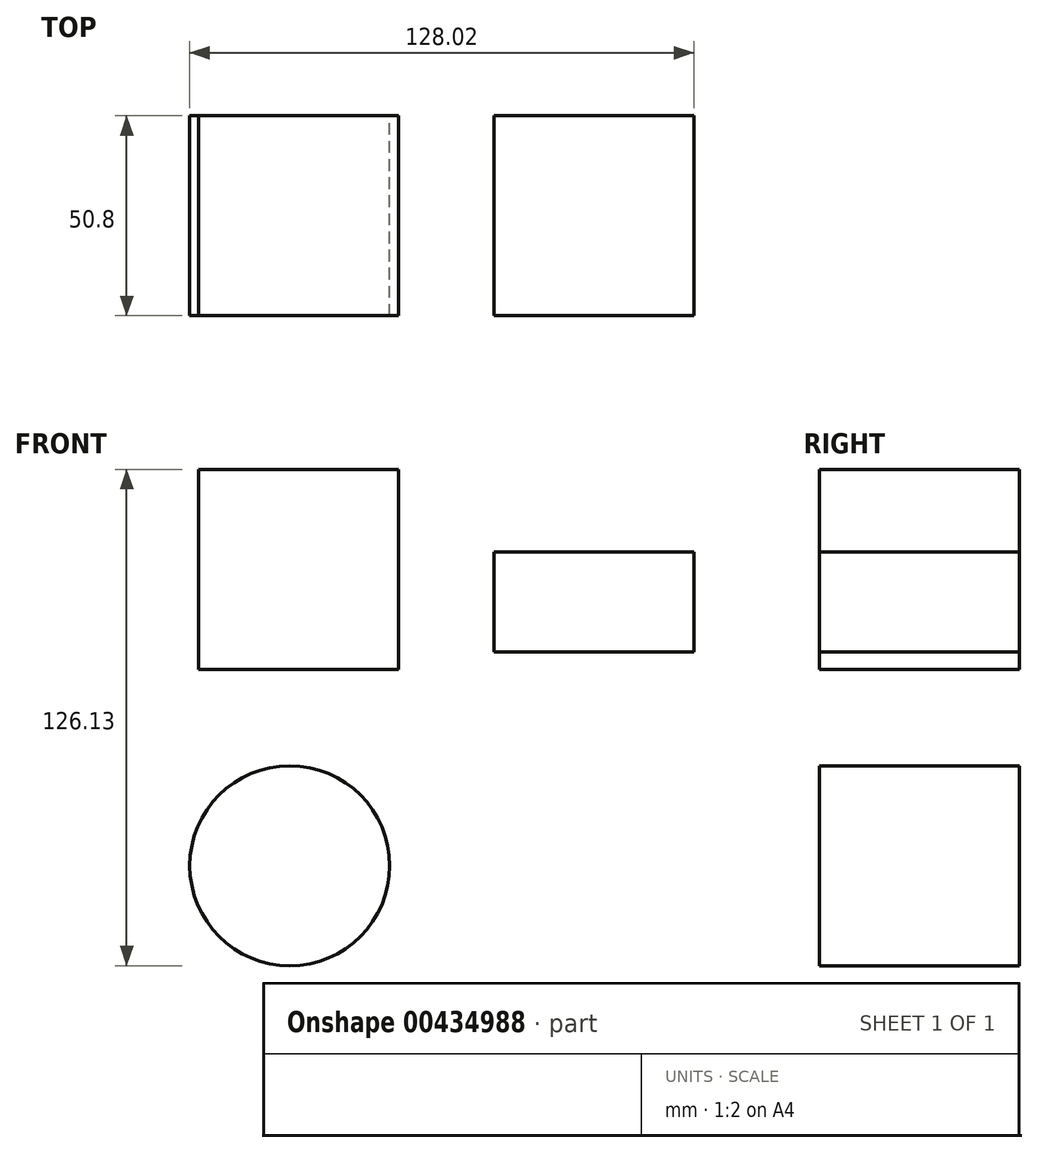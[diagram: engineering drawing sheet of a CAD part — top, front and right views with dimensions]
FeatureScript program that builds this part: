
annotation { "Feature Type Name" : "Feature", "Feature Type Description" : "" }
export const myFeature = defineFeature(function(context is Context, id is Id, definition is map)
    precondition{}
    {
        {
            var Q0;
            Q0=qCreatedBy(makeId("Front.planeOp"),FACE);
            var sketch = newSketch(context, id + "F0", { "sketchPlane" : qUnion([Q0])});
            skLineSegment(sketch, "E0.bottom", {"start": v(-61.8, 66.31) * mm, "end": v(-11, 66.31) * mm});
            skLineSegment(sketch, "E0.top", {"start": v(-61.8, 15.51) * mm, "end": v(-11, 15.51) * mm});
            skLineSegment(sketch, "E0.left", {"start": v(-61.8, 66.31) * mm, "end": v(-61.8, 15.51) * mm});
            skLineSegment(sketch, "E0.right", {"start": v(-11, 66.31) * mm, "end": v(-11, 15.51) * mm});
            skSolve(sketch);
        }
        {
            var Q0;
            Q0=qCreatedBy(makeId("Front.planeOp"),FACE);
            var sketch = newSketch(context, id + "F1", { "sketchPlane" : qUnion([Q0])});
            skLineSegment(sketch, "E1.bottom", {"start": v(13.2, 45.3) * mm, "end": v(64, 45.3) * mm});
            skLineSegment(sketch, "E1.top", {"start": v(13.2, 19.9) * mm, "end": v(64, 19.9) * mm});
            skLineSegment(sketch, "E1.left", {"start": v(13.2, 45.3) * mm, "end": v(13.2, 19.9) * mm});
            skLineSegment(sketch, "E1.right", {"start": v(64, 45.3) * mm, "end": v(64, 19.9) * mm});
            skSolve(sketch);
        }
        {
            var Q0;
            Q0=qCreatedBy(makeId("Front.planeOp"),FACE);
            var sketch = newSketch(context, id + "F2", { "sketchPlane" : qUnion([Q0])});
            skCircle(sketch, "E2", {"center": v(-38.6, -34.42) * mm, "radius": 25.4 * mm});
            skSolve(sketch);
        }
        {
            var Q0;
            Q0 = qSketchRegion(id + "F0", true);
            var Q1;
            Q1=makeQuery(id+"F0.imprint","IMPRINT",FACE,{"disambiguationData":[TD([[makeQuery(id+"F0.imprint","IMPRINT",EDGE,{"derivedFrom":sQuery(id+"F0.wireOp",EDGE,"E0.bottom")}),-1.0]])]});
            extrude(context, id + "F3", {"entities" : qUnion([Q0, Q1]), "depth" : 50.8 * mm});
        }
        {
            var Q0;
            Q0=makeQuery(id+"F1.imprint","IMPRINT",FACE,{"disambiguationData":[TD([[makeQuery(id+"F1.imprint","IMPRINT",EDGE,{"derivedFrom":sQuery(id+"F1.wireOp",EDGE,"E1.bottom")}),-1.0]])]});
            var Q1;
            Q1=makeQuery(id+"F2.imprint","IMPRINT",FACE,{"disambiguationData":[TD([[makeQuery(id+"F2.imprint","IMPRINT",EDGE,{"derivedFrom":sQuery(id+"F2.wireOp",EDGE,"E2")}),1.0]])]});
            extrude(context, id + "F4", {"entities" : qUnion([Q0, Q1]), "depth" : 50.8 * mm});
        }
    });
